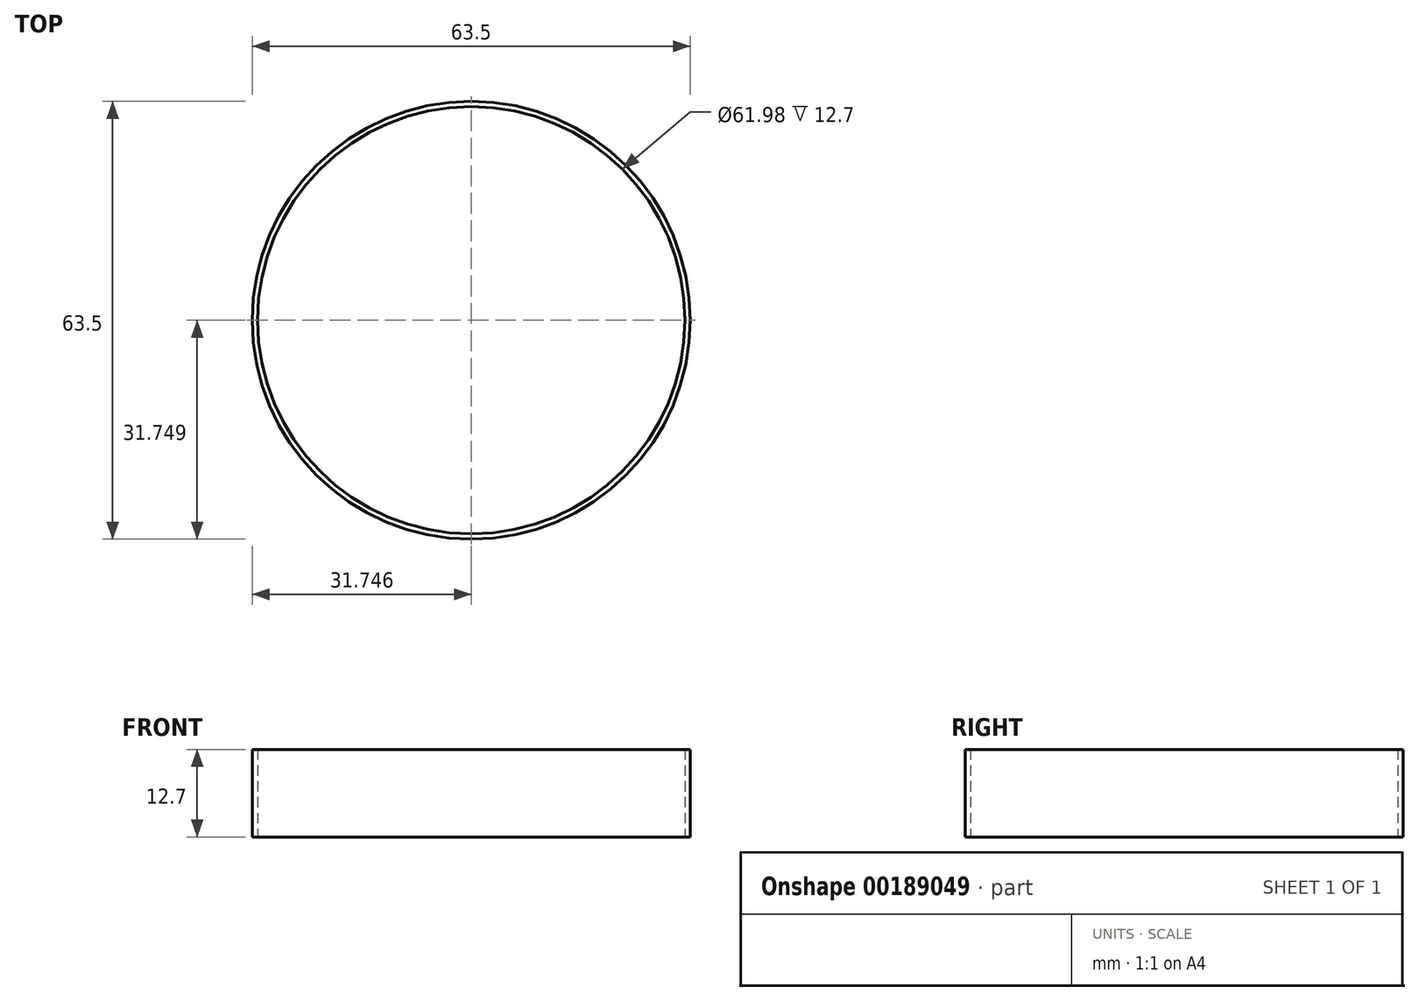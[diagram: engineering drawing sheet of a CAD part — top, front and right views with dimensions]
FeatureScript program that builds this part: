
annotation { "Feature Type Name" : "Feature", "Feature Type Description" : "" }
export const myFeature = defineFeature(function(context is Context, id is Id, definition is map)
    precondition{}
    {
        {
            var Q0;
            Q0=qCreatedBy(makeId("Top.planeOp"),FACE);
            var sketch = newSketch(context, id + "F0", { "sketchPlane" : qUnion([Q0])});
            skCircle(sketch, "E0", {"center": v(0.19, 0.28) * mm, "radius": 30.99 * mm});
            skCircle(sketch, "E1.0", {"center": v(0.19, 0.28) * mm, "radius": 31.75 * mm});
            skSolve(sketch);
        }
        {
            var Q0;
            Q0 = qSketchRegion(id + "F0", true);
            extrude(context, id + "F1", {"entities" : qUnion([Q0]), "depth" : 12.7 * mm});
        }
    });
